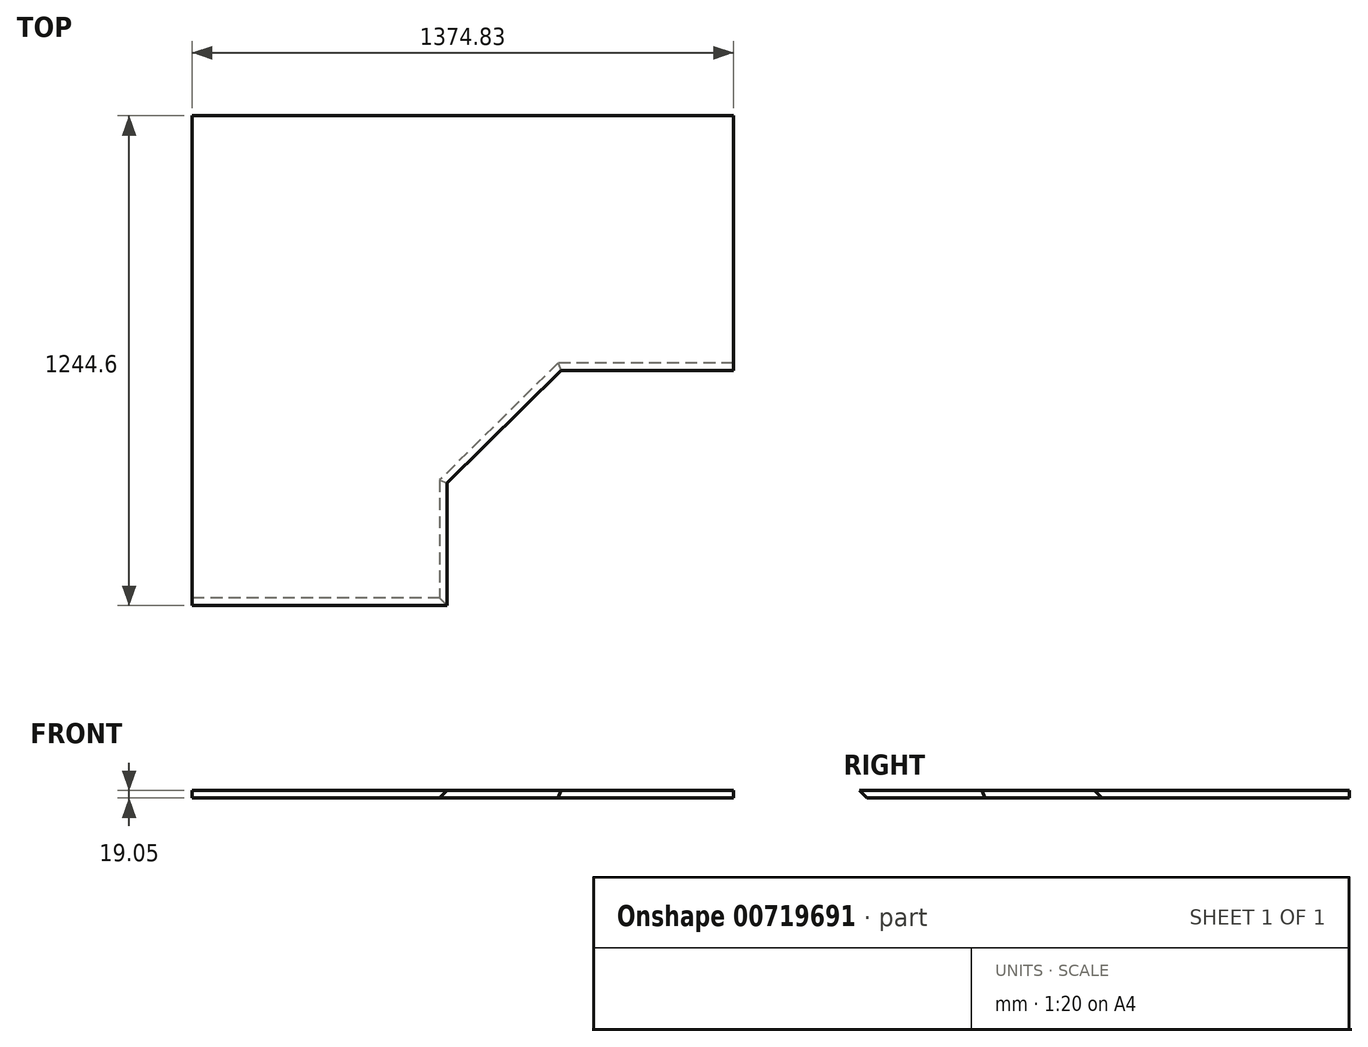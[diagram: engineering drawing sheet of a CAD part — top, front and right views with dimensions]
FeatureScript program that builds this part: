
annotation { "Feature Type Name" : "Feature", "Feature Type Description" : "" }
export const myFeature = defineFeature(function(context is Context, id is Id, definition is map)
    precondition{}
    {
        {
            var Q0;
            Q0=qCreatedBy(makeId("Top.planeOp"),FACE);
            var sketch = newSketch(context, id + "F0", { "sketchPlane" : qUnion([Q0])});
            skLineSegment(sketch, "E0", {"start": v(0, 0) * mm, "end": v(647.7, 0) * mm});
            skLineSegment(sketch, "E1", {"start": v(647.7, 0) * mm, "end": v(647.7, 311.15) * mm});
            skLineSegment(sketch, "E2", {"start": v(647.7, 311.15) * mm, "end": v(936.68, 596.9) * mm});
            skLineSegment(sketch, "E3", {"start": v(936.68, 596.9) * mm, "end": v(1374.83, 596.9) * mm});
            skLineSegment(sketch, "E4", {"start": v(1374.83, 596.9) * mm, "end": v(1374.83, 1244.6) * mm});
            skLineSegment(sketch, "E5", {"start": v(1374.83, 1244.6) * mm, "end": v(0, 1244.6) * mm});
            skLineSegment(sketch, "E6", {"start": v(0, 1244.6) * mm, "end": v(0, 0) * mm});
            skLineSegment(sketch, "E7", {"start": v(647.7, 0) * mm, "end": v(1374.83, 0) * mm, "construction": true});
            skLineSegment(sketch, "E8", {"start": v(1374.83, 0) * mm, "end": v(1374.83, 596.9) * mm, "construction": true});
            skPoint(sketch, "E9", {"position": v(1374.83, 254) * mm});
            skPoint(sketch, "E10", {"position": v(1120.83, 0) * mm});
            skCircle(sketch, "E11", {"center": v(1120.83, 254) * mm, "radius": 254 * mm, "construction": true});
            skSolve(sketch);
        }
        {
            var Q0;
            Q0=makeQuery(id+"F0.imprint","IMPRINT",FACE,{"disambiguationData":[TD([[makeQuery(id+"F0.imprint","IMPRINT",EDGE,{"derivedFrom":sQuery(id+"F0.wireOp",EDGE,"E0")}),1.0]])]});
            extrude(context, id + "F1", {"entities" : qUnion([Q0]), "depth" : 19.05 * mm, "offsetDistance" : 25.4 * mm});
        }
        {
            var Q0;
            Q0=makeQuery(id+"F1.opExtrude","CAP_EDGE",EDGE,{"disambiguationData":[OSD([sQuery(id+"F0.wireOp",EDGE,"E1")])],"isStart":true});
            var Q1;
            Q1=makeQuery(id+"F1.opExtrude","CAP_EDGE",EDGE,{"disambiguationData":[OSD([sQuery(id+"F0.wireOp",EDGE,"E2")])],"isStart":true});
            var Q2;
            Q2=makeQuery(id+"F1.opExtrude","CAP_EDGE",EDGE,{"disambiguationData":[OSD([sQuery(id+"F0.wireOp",EDGE,"E3")])],"isStart":true});
            var Q3;
            Q3=makeQuery(id+"F1.opExtrude","CAP_EDGE",EDGE,{"disambiguationData":[OSD([sQuery(id+"F0.wireOp",EDGE,"E0")])],"isStart":true});
            chamfer(context, id + "F2", {"entities" : qUnion([Q0, Q1, Q2, Q3]), "width" : 19.05 * mm, "tangentPropagation" : true});
        }
    });
